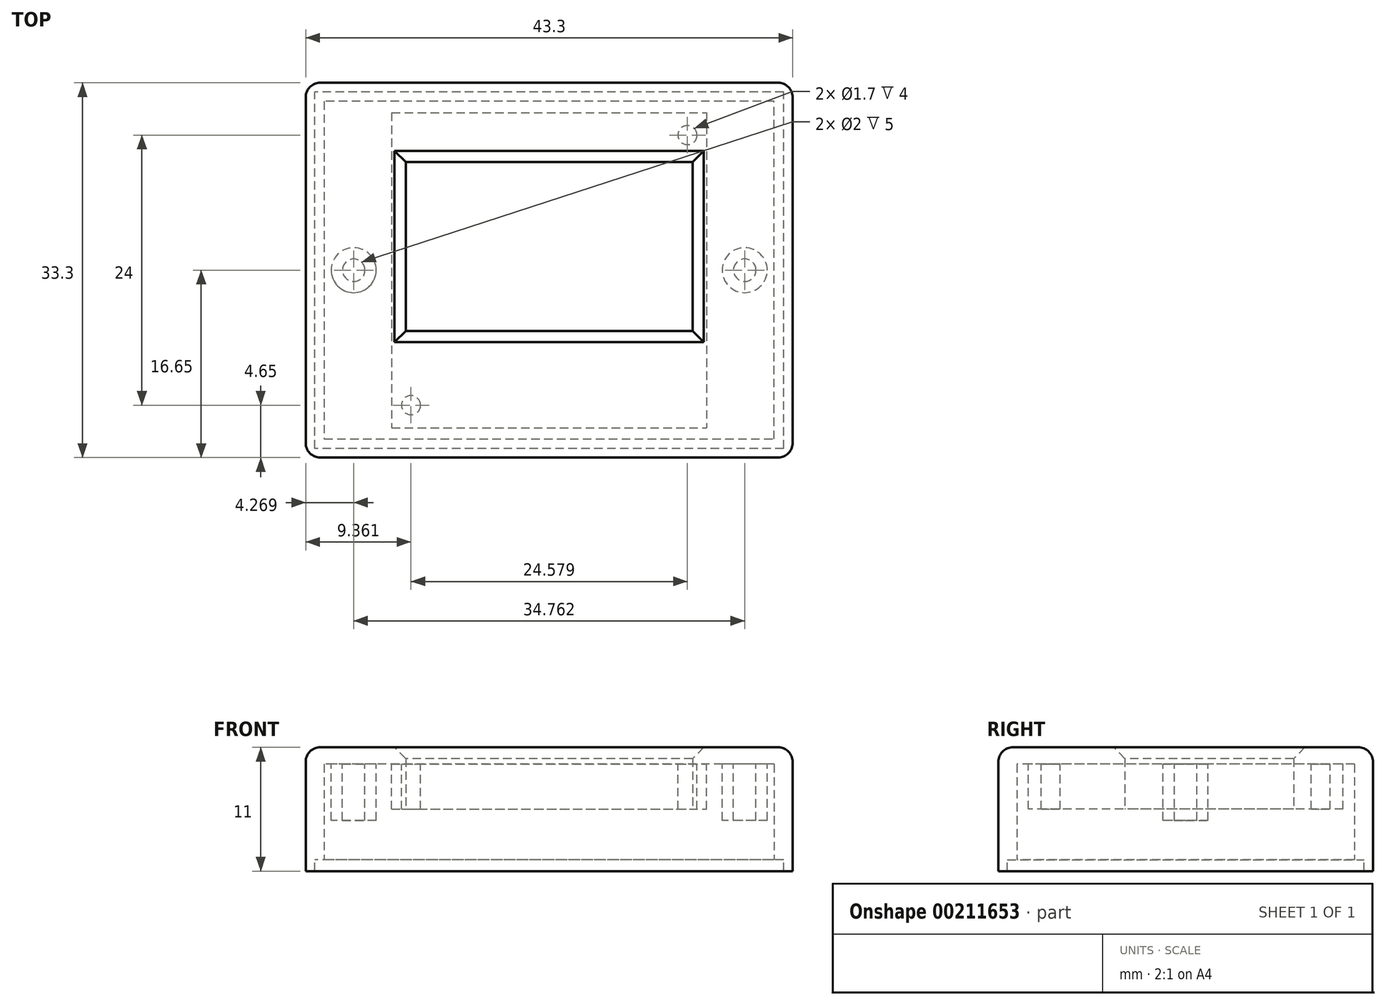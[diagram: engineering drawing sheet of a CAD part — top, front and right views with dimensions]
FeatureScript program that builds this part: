
annotation { "Feature Type Name" : "Feature", "Feature Type Description" : "" }
export const myFeature = defineFeature(function(context is Context, id is Id, definition is map)
    precondition{}
    {
        {
            var Q0;
            Q0=qCreatedBy(makeId("Top.planeOp"),FACE);
            var sketch = newSketch(context, id + "F0", { "sketchPlane" : qUnion([Q0])});
            skPoint(sketch, "E0.middle", {"position": v(0, 0) * mm});
            skLineSegment(sketch, "E1.0", {"start": v(21.65, -16.65) * mm, "end": v(-21.65, -16.65) * mm});
            skLineSegment(sketch, "E1.1", {"start": v(21.65, -16.65) * mm, "end": v(21.65, 16.65) * mm});
            skLineSegment(sketch, "E1.2", {"start": v(21.65, 16.65) * mm, "end": v(-21.65, 16.65) * mm});
            skLineSegment(sketch, "E1.3", {"start": v(-21.65, -16.65) * mm, "end": v(-21.65, 16.65) * mm});
            skSolve(sketch);
        }
        {
            var Q0;
            Q0 = qSketchRegion(id + "F0", true);
            extrude(context, id + "F1", {"entities" : qUnion([Q0]), "depth" : 10 * mm});
        }
        {
            var Q0;
            Q0=makeQuery(id+"F0.imprint","IMPRINT",FACE,{"disambiguationData":[TD([[makeQuery(id+"F0.imprint","IMPRINT",EDGE,{"derivedFrom":sQuery(id+"F0.wireOp",EDGE,"E1.0")}),-1.0]])]});
            var sketch = newSketch(context, id + "F2", { "sketchPlane" : qUnion([Q0])});
            skLineSegment(sketch, "E2.0", {"start": v(-20, 15) * mm, "end": v(-20, -15) * mm});
            skLineSegment(sketch, "E2.1", {"start": v(20, 15) * mm, "end": v(-20, 15) * mm});
            skLineSegment(sketch, "E2.2", {"start": v(20, -15) * mm, "end": v(20, 15) * mm});
            skLineSegment(sketch, "E2.3", {"start": v(-20, -15) * mm, "end": v(20, -15) * mm});
            skSolve(sketch);
        }
        {
            var Q0;
            Q0 = qSketchRegion(id + "F2", true);
            extrude(context, id + "F3", {"entities" : qUnion([Q0]), "operationType" : NewBodyOperationType.REMOVE, "depth" : 8.5 * mm});
        }
        {
            var Q0;
            Q0=makeQuery(id+"F3.boolean.opBoolean","COPY",FACE,{"derivedFrom":makeQuery(id+"F3.opExtrude","CAP_FACE",FACE,{"disambiguationData":[OSD([sQuery(id+"F2.wireOp",EDGE,"E2.0"),sQuery(id+"F2.wireOp",EDGE,"E2.1"),sQuery(id+"F2.wireOp",EDGE,"E2.2"),sQuery(id+"F2.wireOp",EDGE,"E2.3")])],"isStart":false})});
            var sketch = newSketch(context, id + "F4", { "sketchPlane" : qUnion([Q0])});
            skLineSegment(sketch, "E3.bottom", {"start": v(-21.65, 16.65) * mm, "end": v(21.65, 16.65) * mm});
            skLineSegment(sketch, "E3.top", {"start": v(-21.65, -16.65) * mm, "end": v(21.65, -16.65) * mm});
            skLineSegment(sketch, "E3.left", {"start": v(-21.65, 16.65) * mm, "end": v(-21.65, -16.65) * mm});
            skLineSegment(sketch, "E3.right", {"start": v(21.65, 16.65) * mm, "end": v(21.65, -16.65) * mm});
            skLineSegment(sketch, "E4.bottom", {"start": v(-14, -14) * mm, "end": v(14, -14) * mm});
            skLineSegment(sketch, "E4.top", {"start": v(-14, 14) * mm, "end": v(14, 14) * mm});
            skLineSegment(sketch, "E4.left", {"start": v(-14, -14) * mm, "end": v(-14, 14) * mm});
            skLineSegment(sketch, "E4.right", {"start": v(14, -14) * mm, "end": v(14, 14) * mm});
            skPoint(sketch, "E4.middle", {"position": v(0, 0) * mm});
            skLineSegment(sketch, "E5.bottom", {"start": v(-12.75, -9.6) * mm, "end": v(12.75, -9.6) * mm});
            skLineSegment(sketch, "E5.top", {"start": v(-12.75, 5.4) * mm, "end": v(12.75, 5.4) * mm});
            skLineSegment(sketch, "E5.left", {"start": v(-12.75, -9.6) * mm, "end": v(-12.75, 5.4) * mm});
            skLineSegment(sketch, "E5.right", {"start": v(12.75, -9.6) * mm, "end": v(12.75, 5.4) * mm});
            skPoint(sketch, "E6", {"position": v(0, -9.6) * mm});
            skLineSegment(sketch, "E7", {"start": v(0, -15) * mm, "end": v(0, 15) * mm, "construction": true});
            skCircle(sketch, "E8", {"center": v(-12.29, -12) * mm, "radius": 0.85 * mm});
            skLineSegment(sketch, "E9", {"start": v(-21.65, 0) * mm, "end": v(21.65, 0) * mm, "construction": true});
            skCircle(sketch, "E10.MirrorC", {"center": v(-12.29, 12) * mm, "radius": 0.85 * mm});
            skLineSegment(sketch, "E11.MirrorCS", {"start": v(0, 15) * mm, "end": v(0, -15) * mm, "construction": true});
            skCircle(sketch, "E12.MirrorC", {"center": v(12.29, 12) * mm, "radius": 0.85 * mm});
            skCircle(sketch, "E13.MirrorC", {"center": v(12.29, -12) * mm, "radius": 0.85 * mm});
            skSolve(sketch);
        }
        {
            var Q0;
            Q0=makeQuery(id+"F4.imprint","IMPRINT",FACE,{"disambiguationData":[TD([[makeQuery(id+"F4.imprint","IMPRINT",EDGE,{"derivedFrom":sQuery(id+"F4.wireOp",EDGE,"E5.bottom")}),1.0]])]});
            extrude(context, id + "F5", {"entities" : qUnion([Q0]), "operationType" : NewBodyOperationType.REMOVE, "oppositeDirection" : true, "depth" : 25 * mm});
        }
        {
            var Q0;
            Q0=makeQuery(id+"F4.imprint","IMPRINT",FACE,{"disambiguationData":[TD([[makeQuery(id+"F4.imprint","IMPRINT",EDGE,{"derivedFrom":sQuery(id+"F4.wireOp",EDGE,"E12.MirrorC")}),1.0]])]});
            var Q1;
            Q1=makeQuery(id+"F4.imprint","IMPRINT",FACE,{"disambiguationData":[TD([[makeQuery(id+"F4.imprint","IMPRINT",EDGE,{"derivedFrom":sQuery(id+"F4.wireOp",EDGE,"E10.MirrorC")}),-1.0]])]});
            var Q2;
            Q2=makeQuery(id+"F4.imprint","IMPRINT",FACE,{"disambiguationData":[TD([[makeQuery(id+"F4.imprint","IMPRINT",EDGE,{"derivedFrom":sQuery(id+"F4.wireOp",EDGE,"E8")}),1.0]])]});
            var Q3;
            Q3=makeQuery(id+"F4.imprint","IMPRINT",FACE,{"disambiguationData":[TD([[makeQuery(id+"F4.imprint","IMPRINT",EDGE,{"derivedFrom":sQuery(id+"F4.wireOp",EDGE,"E13.MirrorC")}),-1.0]])]});
            extrude(context, id + "F6", {"entities" : qUnion([Q0, Q1, Q2, Q3]), "operationType" : NewBodyOperationType.ADD, "depth" : 4 * mm});
        }
        {
            var Q0;
            Q0=makeQuery(id+"F1.opExtrude","CAP_FACE",FACE,{"disambiguationData":[OSD([sQuery(id+"F0.wireOp",EDGE,"E1.0"),sQuery(id+"F0.wireOp",EDGE,"E1.1"),sQuery(id+"F0.wireOp",EDGE,"E1.2"),sQuery(id+"F0.wireOp",EDGE,"E1.3")])],"isStart":true});
            var sketch = newSketch(context, id + "F7", { "sketchPlane" : qUnion([Q0])});
            skLineSegment(sketch, "E14.0", {"start": v(20.85, 15.85) * mm, "end": v(-20.85, 15.85) * mm});
            skLineSegment(sketch, "E14.1", {"start": v(20.85, 15.85) * mm, "end": v(20.85, -15.85) * mm});
            skLineSegment(sketch, "E14.2", {"start": v(20.85, -15.85) * mm, "end": v(-20.85, -15.85) * mm});
            skLineSegment(sketch, "E14.3", {"start": v(-20.85, 15.85) * mm, "end": v(-20.85, -15.85) * mm});
            skLineSegment(sketch, "E15.bottom", {"start": v(-21.65, 16.65) * mm, "end": v(21.65, 16.65) * mm});
            skLineSegment(sketch, "E15.top", {"start": v(-21.65, -16.65) * mm, "end": v(21.65, -16.65) * mm});
            skLineSegment(sketch, "E15.left", {"start": v(-21.65, 16.65) * mm, "end": v(-21.65, -16.65) * mm});
            skLineSegment(sketch, "E15.right", {"start": v(21.65, 16.65) * mm, "end": v(21.65, -16.65) * mm});
            skSolve(sketch);
        }
        {
            var Q0;
            Q0 = qSketchRegion(id + "F7", true);
            extrude(context, id + "F8", {"entities" : qUnion([Q0]), "operationType" : NewBodyOperationType.ADD, "depth" : 1 * mm});
        }
        {
            var Q0;
            Q0=makeQuery(id+"F4.imprint","IMPRINT",FACE,{"disambiguationData":[TD([[makeQuery(id+"F4.imprint","IMPRINT",EDGE,{"derivedFrom":sQuery(id+"F4.wireOp",EDGE,"E4.bottom")}),-1.0]])]});
            var sketch = newSketch(context, id + "F9", { "sketchPlane" : qUnion([Q0])});
            skCircle(sketch, "E16", {"center": v(-17.38, 0) * mm, "radius": 2 * mm});
            skCircle(sketch, "E17", {"center": v(-17.38, 0) * mm, "radius": 1 * mm});
            skSolve(sketch);
        }
        {
            var Q0;
            Q0 = qSketchRegion(id + "F9", true);
            extrude(context, id + "F10", {"entities" : qUnion([Q0]), "depth" : 5 * mm});
        }
        {
            var Q0;
            Q0=makeQuery(id+"F10.opExtrude","SWEPT_BODY",BODY,{"disambiguationData":[OSD([sQuery(id+"F9.wireOp",EDGE,"E16"),sQuery(id+"F9.wireOp",EDGE,"E17")])]});
            var Q1;
            Q1=qCreatedBy(makeId("Right.planeOp"),FACE);
            mirror(context, id + "F11", {"operationType" : NewBodyOperationType.ADD, "entities" : qUnion([Q0]), "mirrorPlane" : qUnion([Q1])});
        }
        {
            var Q0;
            Q0=makeQuery(id+"F5.boolean.opBoolean","INTERSECT",EDGE,{"derivedFrom":[makeQuery(id+"F1.opExtrude","CAP_FACE",FACE,{"disambiguationData":[OSD([sQuery(id+"F0.wireOp",EDGE,"E1.0"),sQuery(id+"F0.wireOp",EDGE,"E1.1"),sQuery(id+"F0.wireOp",EDGE,"E1.2"),sQuery(id+"F0.wireOp",EDGE,"E1.3")])],"isStart":false}),makeQuery(id+"F5.opExtrude","SWEPT_FACE",FACE,{"disambiguationData":[OSD([sQuery(id+"F4.wireOp",EDGE,"E5.bottom")])]})]});
            var Q1;
            Q1=makeQuery(id+"F5.boolean.opBoolean","INTERSECT",EDGE,{"derivedFrom":[makeQuery(id+"F1.opExtrude","CAP_FACE",FACE,{"disambiguationData":[OSD([sQuery(id+"F0.wireOp",EDGE,"E1.0"),sQuery(id+"F0.wireOp",EDGE,"E1.1"),sQuery(id+"F0.wireOp",EDGE,"E1.2"),sQuery(id+"F0.wireOp",EDGE,"E1.3")])],"isStart":false}),makeQuery(id+"F5.opExtrude","SWEPT_FACE",FACE,{"disambiguationData":[OSD([sQuery(id+"F4.wireOp",EDGE,"E5.left")])]})]});
            var Q2;
            Q2=makeQuery(id+"F5.boolean.opBoolean","INTERSECT",EDGE,{"derivedFrom":[makeQuery(id+"F1.opExtrude","CAP_FACE",FACE,{"disambiguationData":[OSD([sQuery(id+"F0.wireOp",EDGE,"E1.0"),sQuery(id+"F0.wireOp",EDGE,"E1.1"),sQuery(id+"F0.wireOp",EDGE,"E1.2"),sQuery(id+"F0.wireOp",EDGE,"E1.3")])],"isStart":false}),makeQuery(id+"F5.opExtrude","SWEPT_FACE",FACE,{"disambiguationData":[OSD([sQuery(id+"F4.wireOp",EDGE,"E5.top")])]})]});
            var Q3;
            Q3=makeQuery(id+"F5.boolean.opBoolean","INTERSECT",EDGE,{"derivedFrom":[makeQuery(id+"F1.opExtrude","CAP_FACE",FACE,{"disambiguationData":[OSD([sQuery(id+"F0.wireOp",EDGE,"E1.0"),sQuery(id+"F0.wireOp",EDGE,"E1.1"),sQuery(id+"F0.wireOp",EDGE,"E1.2"),sQuery(id+"F0.wireOp",EDGE,"E1.3")])],"isStart":false}),makeQuery(id+"F5.opExtrude","SWEPT_FACE",FACE,{"disambiguationData":[OSD([sQuery(id+"F4.wireOp",EDGE,"E5.right")])]})]});
            chamfer(context, id + "F12", {"entities" : qUnion([Q0, Q1, Q2, Q3]), "width" : 1 * mm, "tangentPropagation" : true});
        }
        {
            var Q0;
            Q0=makeQuery(id+"F8.boolean.opBoolean","MERGE",EDGE,{"derivedFrom":[makeQuery(id+"F1.opExtrude","SWEPT_EDGE",EDGE,{"disambiguationData":[OSD([sQuery(id+"F0.wireOp",EDGE,"E1.2"),sQuery(id+"F0.wireOp",EDGE,"E1.3")])]}),makeQuery(id+"F8.opExtrude","SWEPT_EDGE",EDGE,{"disambiguationData":[OSD([sQuery(id+"F7.wireOp",EDGE,"E15.top"),sQuery(id+"F7.wireOp",EDGE,"E15.left")])]})]});
            var Q1;
            Q1=makeQuery(id+"F8.boolean.opBoolean","MERGE",EDGE,{"derivedFrom":[makeQuery(id+"F1.opExtrude","SWEPT_EDGE",EDGE,{"disambiguationData":[OSD([sQuery(id+"F0.wireOp",EDGE,"E1.1"),sQuery(id+"F0.wireOp",EDGE,"E1.2")])]}),makeQuery(id+"F8.opExtrude","SWEPT_EDGE",EDGE,{"disambiguationData":[OSD([sQuery(id+"F7.wireOp",EDGE,"E15.top"),sQuery(id+"F7.wireOp",EDGE,"E15.right")])]})]});
            var Q2;
            Q2=makeQuery(id+"F8.boolean.opBoolean","MERGE",EDGE,{"derivedFrom":[makeQuery(id+"F1.opExtrude","SWEPT_EDGE",EDGE,{"disambiguationData":[OSD([sQuery(id+"F0.wireOp",EDGE,"E1.0"),sQuery(id+"F0.wireOp",EDGE,"E1.1")])]}),makeQuery(id+"F8.opExtrude","SWEPT_EDGE",EDGE,{"disambiguationData":[OSD([sQuery(id+"F7.wireOp",EDGE,"E15.bottom"),sQuery(id+"F7.wireOp",EDGE,"E15.right")])]})]});
            var Q3;
            Q3=makeQuery(id+"F8.boolean.opBoolean","MERGE",EDGE,{"derivedFrom":[makeQuery(id+"F1.opExtrude","SWEPT_EDGE",EDGE,{"disambiguationData":[OSD([sQuery(id+"F0.wireOp",EDGE,"E1.0"),sQuery(id+"F0.wireOp",EDGE,"E1.3")])]}),makeQuery(id+"F8.opExtrude","SWEPT_EDGE",EDGE,{"disambiguationData":[OSD([sQuery(id+"F7.wireOp",EDGE,"E15.bottom"),sQuery(id+"F7.wireOp",EDGE,"E15.left")])]})]});
            var Q4;
            Q4=makeQuery(id+"F1.opExtrude","CAP_EDGE",EDGE,{"disambiguationData":[OSD([sQuery(id+"F0.wireOp",EDGE,"E1.0")])],"isStart":false});
            var Q5;
            Q5=makeQuery(id+"F1.opExtrude","CAP_EDGE",EDGE,{"disambiguationData":[OSD([sQuery(id+"F0.wireOp",EDGE,"E1.3")])],"isStart":false});
            var Q6;
            Q6=makeQuery(id+"F1.opExtrude","CAP_EDGE",EDGE,{"disambiguationData":[OSD([sQuery(id+"F0.wireOp",EDGE,"E1.1")])],"isStart":false});
            var Q7;
            Q7=makeQuery(id+"F1.opExtrude","CAP_EDGE",EDGE,{"disambiguationData":[OSD([sQuery(id+"F0.wireOp",EDGE,"E1.2")])],"isStart":false});
            fillet(context, id + "F13", {"entities" : qUnion([Q0, Q1, Q2, Q3, Q4, Q5, Q6, Q7]), "radius" : 1.3 * mm, "tangentPropagation" : true, "allowEdgeOverflow" : false});
        }
    });
